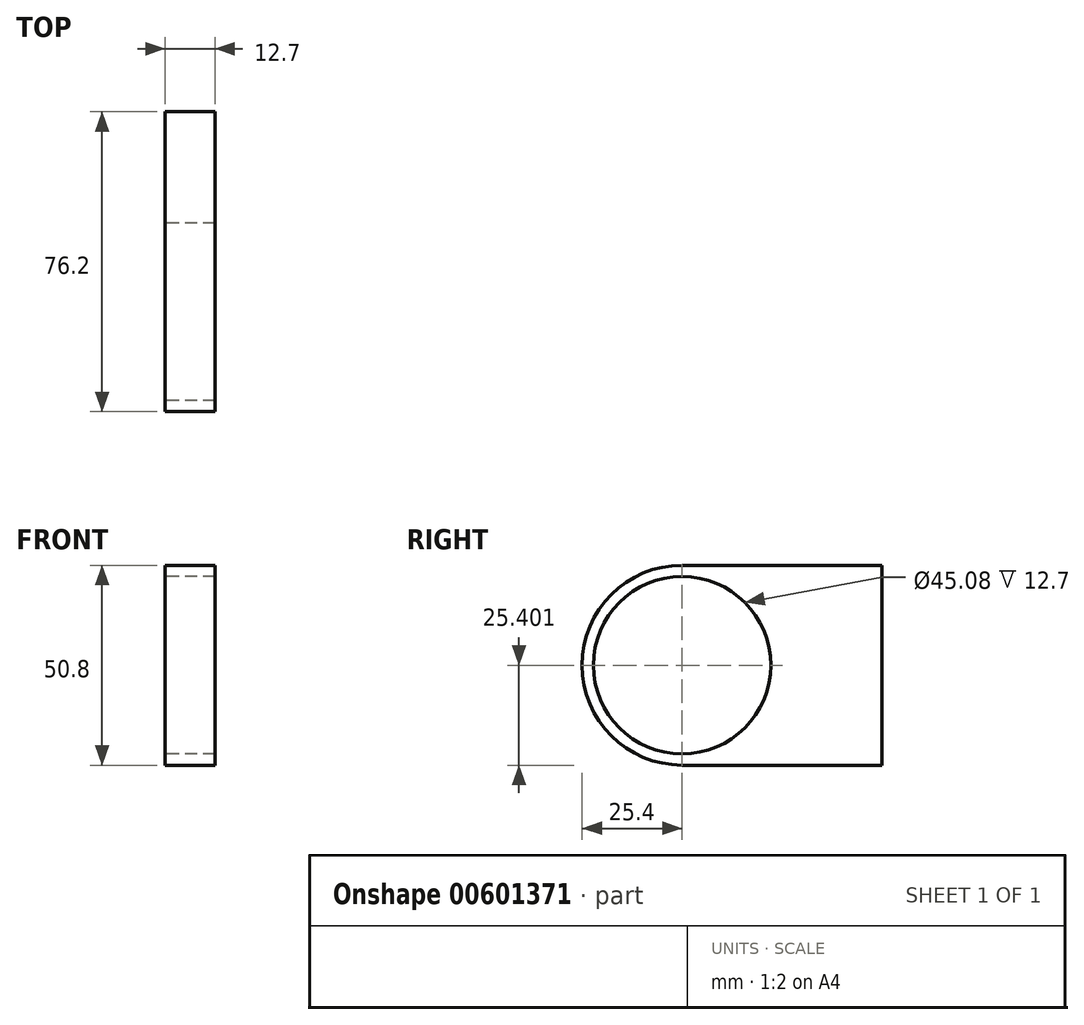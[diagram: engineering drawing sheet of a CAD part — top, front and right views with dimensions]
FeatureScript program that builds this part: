
annotation { "Feature Type Name" : "Feature", "Feature Type Description" : "" }
export const myFeature = defineFeature(function(context is Context, id is Id, definition is map)
    precondition{}
    {
        {
            var Q0;
            Q0=qCreatedBy(makeId("Right.planeOp"),FACE);
            var sketch = newSketch(context, id + "F0", { "sketchPlane" : qUnion([Q0])});
            skLineSegment(sketch, "E0", {"start": v(0, 41.94) * mm, "end": v(-50.8, 41.94) * mm});
            skLineSegment(sketch, "E1", {"start": v(0, 41.94) * mm, "end": v(0, -8.86) * mm});
            skLineSegment(sketch, "E2", {"start": v(0, -8.86) * mm, "end": v(-50.8, -8.86) * mm});
            skLineSegment(sketch, "E3", {"start": v(-50.8, 41.94) * mm, "end": v(-50.8, -8.86) * mm, "construction": true});
            skCircle(sketch, "E4", {"center": v(-50.8, 16.54) * mm, "radius": 25.4 * mm});
            skArc(sketch, "E5", {"start": v(-50.8, 39.08) * mm, "mid": v(-73.34, 16.54) * mm, "end": v(-50.8, -6) * mm});
            skArc(sketch, "E6", {"start": v(-50.8, -6) * mm, "mid": v(-28.26, 16.54) * mm, "end": v(-50.8, 39.08) * mm});
            skSolve(sketch);
        }
        {
            var Q0;
            Q0 = qSketchRegion(id + "F0", true);
            extrude(context, id + "F1", {"entities" : qUnion([Q0]), "depth" : 12.7 * mm, "offsetDistance" : 25.4 * mm});
        }
    });
